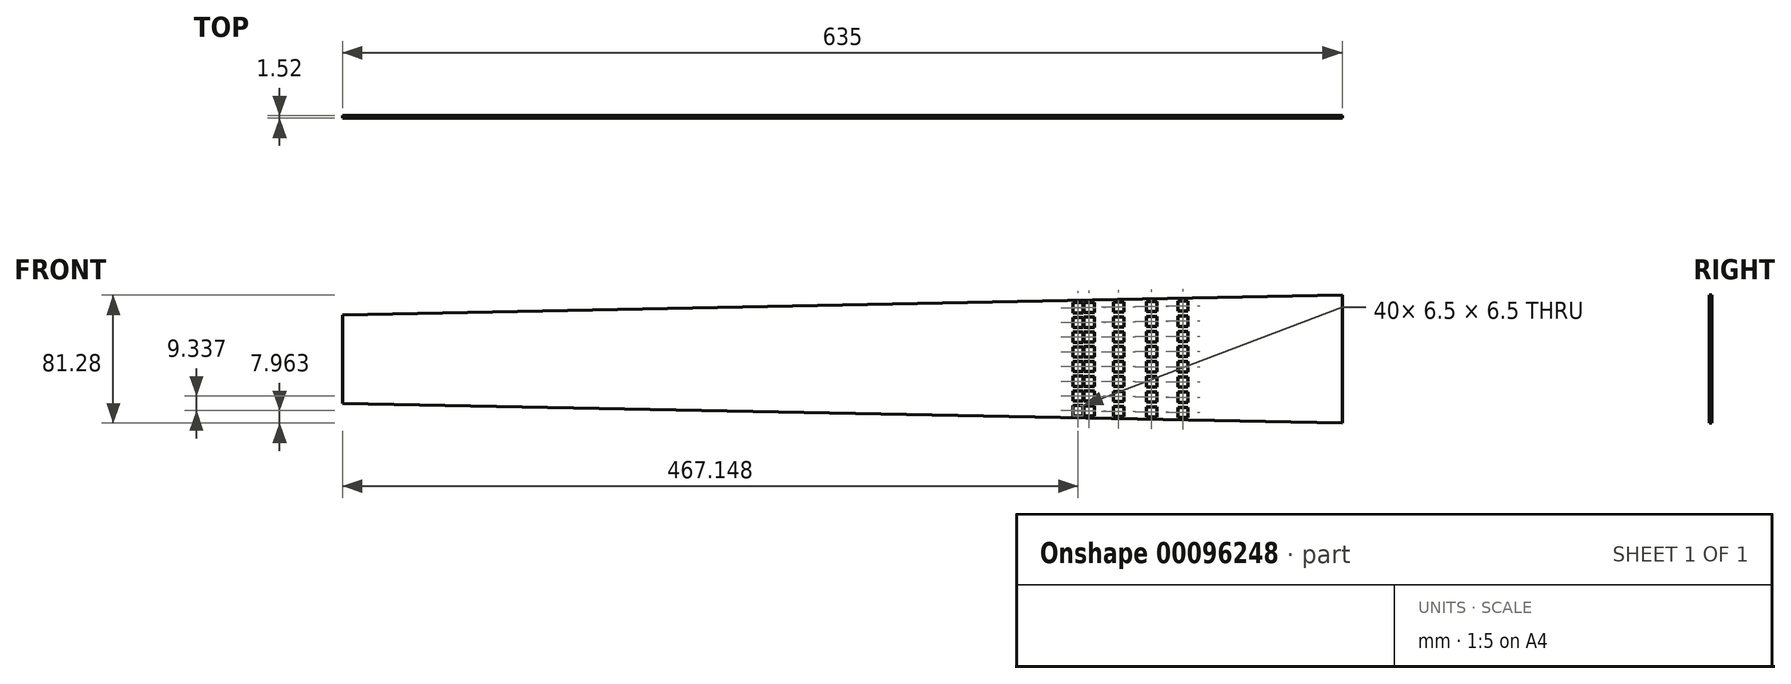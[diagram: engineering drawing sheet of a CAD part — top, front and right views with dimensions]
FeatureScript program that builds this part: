
annotation { "Feature Type Name" : "Feature", "Feature Type Description" : "" }
export const myFeature = defineFeature(function(context is Context, id is Id, definition is map)
    precondition{}
    {
        {
            var Q0;
            Q0=qCreatedBy(makeId("Front.planeOp"),FACE);
            var sketch = newSketch(context, id + "F0", { "sketchPlane" : qUnion([Q0])});
            skLineSegment(sketch, "E0", {"start": v(0, 0) * mm, "end": v(0, 56.39) * mm});
            skLineSegment(sketch, "E1", {"start": v(0, 56.39) * mm, "end": v(304.8, 62.36) * mm});
            skLineSegment(sketch, "E2", {"start": v(635, 68.83) * mm, "end": v(635, -12.45) * mm});
            skLineSegment(sketch, "E3", {"start": v(635, -12.45) * mm, "end": v(304.8, -5.97) * mm});
            skLineSegment(sketch, "E4", {"start": v(0, 28.2) * mm, "end": v(897.35, 28.2) * mm, "construction": true});
            skLineSegment(sketch, "E5", {"start": v(0, 3.52) * mm, "end": v(635, -7.37) * mm, "construction": true});
            skLineSegment(sketch, "E6", {"start": v(0, 10.57) * mm, "end": v(635, 2.8) * mm, "construction": true});
            skLineSegment(sketch, "E7", {"start": v(0, 17.62) * mm, "end": v(635, 12.95) * mm, "construction": true});
            skLineSegment(sketch, "E8", {"start": v(0, 24.67) * mm, "end": v(635, 23.11) * mm, "construction": true});
            skLineSegment(sketch, "E9", {"start": v(467.15, -27.86) * mm, "end": v(467.15, 72.83) * mm, "construction": true});
            skLineSegment(sketch, "E10", {"start": v(492.88, -29.16) * mm, "end": v(492.88, 78.06) * mm, "construction": true});
            skLineSegment(sketch, "E11", {"start": v(513.87, -22.04) * mm, "end": v(513.87, 76.59) * mm, "construction": true});
            skLineSegment(sketch, "E12", {"start": v(533.67, -25.93) * mm, "end": v(533.67, 79.32) * mm, "construction": true});
            skLineSegment(sketch, "E13", {"start": v(586.67, -17.8) * mm, "end": v(586.67, 83.9) * mm, "construction": true});
            skLineSegment(sketch, "E14", {"start": v(552.37, -18.5) * mm, "end": v(552.37, 94.16) * mm, "construction": true});
            skPoint(sketch, "E15", {"position": v(533.67, -5.63) * mm});
            skPoint(sketch, "E16", {"position": v(492.88, -4.93) * mm});
            skLineSegment(sketch, "E17.bottom", {"start": v(489.63, -1.68) * mm, "end": v(496.13, -1.68) * mm});
            skLineSegment(sketch, "E17.top", {"start": v(489.63, -8.18) * mm, "end": v(496.13, -8.18) * mm});
            skLineSegment(sketch, "E17.left", {"start": v(489.63, -1.68) * mm, "end": v(489.63, -8.18) * mm});
            skLineSegment(sketch, "E17.right", {"start": v(496.13, -1.68) * mm, "end": v(496.13, -8.18) * mm});
            skPoint(sketch, "E18", {"position": v(513.87, -5.29) * mm});
            skLineSegment(sketch, "E19.bottom", {"start": v(510.62, -2.04) * mm, "end": v(517.12, -2.04) * mm});
            skLineSegment(sketch, "E19.top", {"start": v(510.62, -8.54) * mm, "end": v(517.12, -8.54) * mm});
            skLineSegment(sketch, "E19.left", {"start": v(510.62, -2.04) * mm, "end": v(510.62, -8.54) * mm});
            skLineSegment(sketch, "E19.right", {"start": v(517.12, -2.04) * mm, "end": v(517.12, -8.54) * mm});
            skLineSegment(sketch, "E20.bottom", {"start": v(530.42, -2.38) * mm, "end": v(536.92, -2.38) * mm});
            skLineSegment(sketch, "E20.top", {"start": v(530.42, -8.88) * mm, "end": v(536.92, -8.88) * mm});
            skLineSegment(sketch, "E20.left", {"start": v(530.42, -2.38) * mm, "end": v(530.42, -8.88) * mm});
            skLineSegment(sketch, "E20.right", {"start": v(536.92, -2.38) * mm, "end": v(536.92, -8.88) * mm});
            skLineSegment(sketch, "E21", {"start": v(304.8, -5.97) * mm, "end": v(304.8, 62.36) * mm});
            skLineSegment(sketch, "E22", {"start": v(211.87, -18.15) * mm, "end": v(211.87, 88.54) * mm, "construction": true});
            skLineSegment(sketch, "E23", {"start": v(248.18, -17.72) * mm, "end": v(248.18, 84.91) * mm, "construction": true});
            skLineSegment(sketch, "E24", {"start": v(304.8, 62.36) * mm, "end": v(635, 68.83) * mm});
            skLineSegment(sketch, "E25", {"start": v(304.8, -5.97) * mm, "end": v(0, 0) * mm});
            skLineSegment(sketch, "E26", {"start": v(474.15, -18.13) * mm, "end": v(474.15, 73.32) * mm, "construction": true});
            skPoint(sketch, "E27", {"position": v(467.15, -4.49) * mm});
            skPoint(sketch, "E28", {"position": v(474.15, -4.6) * mm});
            skLineSegment(sketch, "E29.bottom", {"start": v(463.9, -1.24) * mm, "end": v(470.4, -1.24) * mm});
            skLineSegment(sketch, "E29.top", {"start": v(463.9, -7.74) * mm, "end": v(470.4, -7.74) * mm});
            skLineSegment(sketch, "E29.left", {"start": v(463.9, -1.24) * mm, "end": v(463.9, -7.74) * mm});
            skLineSegment(sketch, "E29.right", {"start": v(470.4, -1.24) * mm, "end": v(470.4, -7.74) * mm});
            skLineSegment(sketch, "E30.bottom", {"start": v(470.9, -1.36) * mm, "end": v(477.4, -1.36) * mm});
            skLineSegment(sketch, "E30.top", {"start": v(470.9, -7.86) * mm, "end": v(477.4, -7.86) * mm});
            skLineSegment(sketch, "E30.left", {"start": v(470.9, -1.36) * mm, "end": v(470.9, -7.86) * mm});
            skLineSegment(sketch, "E30.right", {"start": v(477.4, -1.36) * mm, "end": v(477.4, -7.86) * mm});
            skPoint(sketch, "E31", {"position": v(467.15, 4.85) * mm});
            skPoint(sketch, "E32", {"position": v(474.15, 4.76) * mm});
            skPoint(sketch, "E33", {"position": v(492.88, 4.53) * mm});
            skPoint(sketch, "E34", {"position": v(513.87, 4.28) * mm});
            skPoint(sketch, "E35", {"position": v(533.67, 4.04) * mm});
            skLineSegment(sketch, "E36.direction1", {"start": v(613.98, -10.31) * mm, "end": v(639.38, -10.31) * mm, "construction": true});
            skLineSegment(sketch, "E37.direction1", {"start": v(439.66, -0.82) * mm, "end": v(465.06, -0.82) * mm, "construction": true});
            skLineSegment(sketch, "E38.direction1", {"start": v(448.02, -7.47) * mm, "end": v(473.42, -7.47) * mm, "construction": true});
            skLineSegment(sketch, "E39.0.1.0", {"start": v(463.9, 8.1) * mm, "end": v(463.9, 1.6) * mm});
            skLineSegment(sketch, "E39.0.1.1", {"start": v(463.9, 1.6) * mm, "end": v(470.4, 1.6) * mm});
            skLineSegment(sketch, "E39.0.1.2", {"start": v(470.4, 8.1) * mm, "end": v(470.4, 1.6) * mm});
            skLineSegment(sketch, "E39.0.1.3", {"start": v(463.9, 8.1) * mm, "end": v(470.4, 8.1) * mm});
            skLineSegment(sketch, "E39.0.2.0", {"start": v(463.9, 17.44) * mm, "end": v(463.9, 10.94) * mm});
            skLineSegment(sketch, "E39.0.2.1", {"start": v(463.9, 10.94) * mm, "end": v(470.4, 10.94) * mm});
            skLineSegment(sketch, "E39.0.2.2", {"start": v(470.4, 17.44) * mm, "end": v(470.4, 10.94) * mm});
            skLineSegment(sketch, "E39.0.2.3", {"start": v(463.9, 17.44) * mm, "end": v(470.4, 17.44) * mm});
            skLineSegment(sketch, "E39.0.3.0", {"start": v(463.9, 26.77) * mm, "end": v(463.9, 20.27) * mm});
            skLineSegment(sketch, "E39.0.3.1", {"start": v(463.9, 20.27) * mm, "end": v(470.4, 20.27) * mm});
            skLineSegment(sketch, "E39.0.3.2", {"start": v(470.4, 26.77) * mm, "end": v(470.4, 20.27) * mm});
            skLineSegment(sketch, "E39.0.3.3", {"start": v(463.9, 26.77) * mm, "end": v(470.4, 26.77) * mm});
            skLineSegment(sketch, "E39.0.4.0", {"start": v(463.9, 36.11) * mm, "end": v(463.9, 29.61) * mm});
            skLineSegment(sketch, "E39.0.4.1", {"start": v(463.9, 29.61) * mm, "end": v(470.4, 29.61) * mm});
            skLineSegment(sketch, "E39.0.4.2", {"start": v(470.4, 36.11) * mm, "end": v(470.4, 29.61) * mm});
            skLineSegment(sketch, "E39.0.4.3", {"start": v(463.9, 36.11) * mm, "end": v(470.4, 36.11) * mm});
            skLineSegment(sketch, "E39.0.5.0", {"start": v(463.9, 45.45) * mm, "end": v(463.9, 38.95) * mm});
            skLineSegment(sketch, "E39.0.5.1", {"start": v(463.9, 38.95) * mm, "end": v(470.4, 38.95) * mm});
            skLineSegment(sketch, "E39.0.5.2", {"start": v(470.4, 45.45) * mm, "end": v(470.4, 38.95) * mm});
            skLineSegment(sketch, "E39.0.5.3", {"start": v(463.9, 45.45) * mm, "end": v(470.4, 45.45) * mm});
            skLineSegment(sketch, "E39.0.6.0", {"start": v(463.9, 54.78) * mm, "end": v(463.9, 48.28) * mm});
            skLineSegment(sketch, "E39.0.6.1", {"start": v(463.9, 48.28) * mm, "end": v(470.4, 48.28) * mm});
            skLineSegment(sketch, "E39.0.6.2", {"start": v(470.4, 54.78) * mm, "end": v(470.4, 48.28) * mm});
            skLineSegment(sketch, "E39.0.6.3", {"start": v(463.9, 54.78) * mm, "end": v(470.4, 54.78) * mm});
            skLineSegment(sketch, "E39.0.7.0", {"start": v(463.9, 64.12) * mm, "end": v(463.9, 57.62) * mm});
            skLineSegment(sketch, "E39.0.7.1", {"start": v(463.9, 57.62) * mm, "end": v(470.4, 57.62) * mm});
            skLineSegment(sketch, "E39.0.7.2", {"start": v(470.4, 64.12) * mm, "end": v(470.4, 57.62) * mm});
            skLineSegment(sketch, "E39.0.7.3", {"start": v(463.9, 64.12) * mm, "end": v(470.4, 64.12) * mm});
            skLineSegment(sketch, "E39.direction1", {"start": v(463.9, -7.74) * mm, "end": v(489.3, -7.74) * mm, "construction": true});
            skLineSegment(sketch, "E39.direction2", {"start": v(463.9, -7.74) * mm, "end": v(463.9, 1.6) * mm, "construction": true});
            skLineSegment(sketch, "E40.0.1.0", {"start": v(470.9, 8.02) * mm, "end": v(470.9, 1.52) * mm});
            skLineSegment(sketch, "E40.0.1.1", {"start": v(470.9, 8.02) * mm, "end": v(477.4, 8.02) * mm});
            skLineSegment(sketch, "E40.0.1.2", {"start": v(477.4, 8.02) * mm, "end": v(477.4, 1.52) * mm});
            skLineSegment(sketch, "E40.0.1.3", {"start": v(470.9, 1.52) * mm, "end": v(477.4, 1.52) * mm});
            skLineSegment(sketch, "E40.0.2.0", {"start": v(470.9, 17.39) * mm, "end": v(470.9, 10.89) * mm});
            skLineSegment(sketch, "E40.0.2.1", {"start": v(470.9, 17.39) * mm, "end": v(477.4, 17.39) * mm});
            skLineSegment(sketch, "E40.0.2.2", {"start": v(477.4, 17.39) * mm, "end": v(477.4, 10.89) * mm});
            skLineSegment(sketch, "E40.0.2.3", {"start": v(470.9, 10.89) * mm, "end": v(477.4, 10.89) * mm});
            skLineSegment(sketch, "E40.0.3.0", {"start": v(470.9, 26.76) * mm, "end": v(470.9, 20.26) * mm});
            skLineSegment(sketch, "E40.0.3.1", {"start": v(470.9, 26.76) * mm, "end": v(477.4, 26.76) * mm});
            skLineSegment(sketch, "E40.0.3.2", {"start": v(477.4, 26.76) * mm, "end": v(477.4, 20.26) * mm});
            skLineSegment(sketch, "E40.0.3.3", {"start": v(470.9, 20.26) * mm, "end": v(477.4, 20.26) * mm});
            skLineSegment(sketch, "E40.0.4.0", {"start": v(470.9, 36.13) * mm, "end": v(470.9, 29.63) * mm});
            skLineSegment(sketch, "E40.0.4.1", {"start": v(470.9, 36.13) * mm, "end": v(477.4, 36.13) * mm});
            skLineSegment(sketch, "E40.0.4.2", {"start": v(477.4, 36.13) * mm, "end": v(477.4, 29.63) * mm});
            skLineSegment(sketch, "E40.0.4.3", {"start": v(470.9, 29.63) * mm, "end": v(477.4, 29.63) * mm});
            skLineSegment(sketch, "E40.0.5.0", {"start": v(470.9, 45.5) * mm, "end": v(470.9, 39) * mm});
            skLineSegment(sketch, "E40.0.5.1", {"start": v(470.9, 45.5) * mm, "end": v(477.4, 45.5) * mm});
            skLineSegment(sketch, "E40.0.5.2", {"start": v(477.4, 45.5) * mm, "end": v(477.4, 39) * mm});
            skLineSegment(sketch, "E40.0.5.3", {"start": v(470.9, 39) * mm, "end": v(477.4, 39) * mm});
            skLineSegment(sketch, "E40.0.6.0", {"start": v(470.9, 54.88) * mm, "end": v(470.9, 48.38) * mm});
            skLineSegment(sketch, "E40.0.6.1", {"start": v(470.9, 54.88) * mm, "end": v(477.4, 54.88) * mm});
            skLineSegment(sketch, "E40.0.6.2", {"start": v(477.4, 54.88) * mm, "end": v(477.4, 48.38) * mm});
            skLineSegment(sketch, "E40.0.6.3", {"start": v(470.9, 48.38) * mm, "end": v(477.4, 48.38) * mm});
            skLineSegment(sketch, "E40.0.7.0", {"start": v(470.9, 64.25) * mm, "end": v(470.9, 57.75) * mm});
            skLineSegment(sketch, "E40.0.7.1", {"start": v(470.9, 64.25) * mm, "end": v(477.4, 64.25) * mm});
            skLineSegment(sketch, "E40.0.7.2", {"start": v(477.4, 64.25) * mm, "end": v(477.4, 57.75) * mm});
            skLineSegment(sketch, "E40.0.7.3", {"start": v(470.9, 57.75) * mm, "end": v(477.4, 57.75) * mm});
            skLineSegment(sketch, "E40.direction1", {"start": v(470.9, -7.86) * mm, "end": v(496.3, -7.86) * mm, "construction": true});
            skLineSegment(sketch, "E40.direction2", {"start": v(470.9, -7.86) * mm, "end": v(470.9, 1.52) * mm, "construction": true});
            skLineSegment(sketch, "E41.0.1.0", {"start": v(489.63, 7.79) * mm, "end": v(489.63, 1.29) * mm});
            skLineSegment(sketch, "E41.0.1.1", {"start": v(496.13, 7.79) * mm, "end": v(496.13, 1.29) * mm});
            skLineSegment(sketch, "E41.0.1.2", {"start": v(489.63, 7.79) * mm, "end": v(496.13, 7.79) * mm});
            skLineSegment(sketch, "E41.0.1.3", {"start": v(489.63, 1.29) * mm, "end": v(496.13, 1.29) * mm});
            skLineSegment(sketch, "E41.0.2.0", {"start": v(489.63, 17.25) * mm, "end": v(489.63, 10.75) * mm});
            skLineSegment(sketch, "E41.0.2.1", {"start": v(496.13, 17.25) * mm, "end": v(496.13, 10.75) * mm});
            skLineSegment(sketch, "E41.0.2.2", {"start": v(489.63, 17.25) * mm, "end": v(496.13, 17.25) * mm});
            skLineSegment(sketch, "E41.0.2.3", {"start": v(489.63, 10.75) * mm, "end": v(496.13, 10.75) * mm});
            skLineSegment(sketch, "E41.0.3.0", {"start": v(489.63, 26.71) * mm, "end": v(489.63, 20.21) * mm});
            skLineSegment(sketch, "E41.0.3.1", {"start": v(496.13, 26.71) * mm, "end": v(496.13, 20.21) * mm});
            skLineSegment(sketch, "E41.0.3.2", {"start": v(489.63, 26.71) * mm, "end": v(496.13, 26.71) * mm});
            skLineSegment(sketch, "E41.0.3.3", {"start": v(489.63, 20.21) * mm, "end": v(496.13, 20.21) * mm});
            skLineSegment(sketch, "E41.0.4.0", {"start": v(489.63, 36.18) * mm, "end": v(489.63, 29.68) * mm});
            skLineSegment(sketch, "E41.0.4.1", {"start": v(496.13, 36.18) * mm, "end": v(496.13, 29.68) * mm});
            skLineSegment(sketch, "E41.0.4.2", {"start": v(489.63, 36.18) * mm, "end": v(496.13, 36.18) * mm});
            skLineSegment(sketch, "E41.0.4.3", {"start": v(489.63, 29.68) * mm, "end": v(496.13, 29.68) * mm});
            skLineSegment(sketch, "E41.0.5.0", {"start": v(489.63, 45.64) * mm, "end": v(489.63, 39.14) * mm});
            skLineSegment(sketch, "E41.0.5.1", {"start": v(496.13, 45.64) * mm, "end": v(496.13, 39.14) * mm});
            skLineSegment(sketch, "E41.0.5.2", {"start": v(489.63, 45.64) * mm, "end": v(496.13, 45.64) * mm});
            skLineSegment(sketch, "E41.0.5.3", {"start": v(489.63, 39.14) * mm, "end": v(496.13, 39.14) * mm});
            skLineSegment(sketch, "E41.0.6.0", {"start": v(489.63, 55.1) * mm, "end": v(489.63, 48.6) * mm});
            skLineSegment(sketch, "E41.0.6.1", {"start": v(496.13, 55.1) * mm, "end": v(496.13, 48.6) * mm});
            skLineSegment(sketch, "E41.0.6.2", {"start": v(489.63, 55.1) * mm, "end": v(496.13, 55.1) * mm});
            skLineSegment(sketch, "E41.0.6.3", {"start": v(489.63, 48.6) * mm, "end": v(496.13, 48.6) * mm});
            skLineSegment(sketch, "E41.0.7.0", {"start": v(489.63, 64.57) * mm, "end": v(489.63, 58.07) * mm});
            skLineSegment(sketch, "E41.0.7.1", {"start": v(496.13, 64.57) * mm, "end": v(496.13, 58.07) * mm});
            skLineSegment(sketch, "E41.0.7.2", {"start": v(489.63, 64.57) * mm, "end": v(496.13, 64.57) * mm});
            skLineSegment(sketch, "E41.0.7.3", {"start": v(489.63, 58.07) * mm, "end": v(496.13, 58.07) * mm});
            skLineSegment(sketch, "E41.direction1", {"start": v(489.63, -8.18) * mm, "end": v(515.03, -8.18) * mm, "construction": true});
            skLineSegment(sketch, "E41.direction2", {"start": v(489.63, -8.18) * mm, "end": v(489.63, 1.29) * mm, "construction": true});
            skLineSegment(sketch, "E42.0.1.0", {"start": v(510.62, 7.53) * mm, "end": v(510.62, 1.03) * mm});
            skLineSegment(sketch, "E42.0.1.1", {"start": v(510.62, 7.53) * mm, "end": v(517.12, 7.53) * mm});
            skLineSegment(sketch, "E42.0.1.2", {"start": v(510.62, 1.03) * mm, "end": v(517.12, 1.03) * mm});
            skLineSegment(sketch, "E42.0.1.3", {"start": v(517.12, 7.53) * mm, "end": v(517.12, 1.03) * mm});
            skLineSegment(sketch, "E42.0.2.0", {"start": v(510.62, 17.1) * mm, "end": v(510.62, 10.6) * mm});
            skLineSegment(sketch, "E42.0.2.1", {"start": v(510.62, 17.1) * mm, "end": v(517.12, 17.1) * mm});
            skLineSegment(sketch, "E42.0.2.2", {"start": v(510.62, 10.6) * mm, "end": v(517.12, 10.6) * mm});
            skLineSegment(sketch, "E42.0.2.3", {"start": v(517.12, 17.1) * mm, "end": v(517.12, 10.6) * mm});
            skLineSegment(sketch, "E42.0.3.0", {"start": v(510.62, 26.66) * mm, "end": v(510.62, 20.16) * mm});
            skLineSegment(sketch, "E42.0.3.1", {"start": v(510.62, 26.66) * mm, "end": v(517.12, 26.66) * mm});
            skLineSegment(sketch, "E42.0.3.2", {"start": v(510.62, 20.16) * mm, "end": v(517.12, 20.16) * mm});
            skLineSegment(sketch, "E42.0.3.3", {"start": v(517.12, 26.66) * mm, "end": v(517.12, 20.16) * mm});
            skLineSegment(sketch, "E42.0.4.0", {"start": v(510.62, 36.22) * mm, "end": v(510.62, 29.72) * mm});
            skLineSegment(sketch, "E42.0.4.1", {"start": v(510.62, 36.22) * mm, "end": v(517.12, 36.22) * mm});
            skLineSegment(sketch, "E42.0.4.2", {"start": v(510.62, 29.72) * mm, "end": v(517.12, 29.72) * mm});
            skLineSegment(sketch, "E42.0.4.3", {"start": v(517.12, 36.22) * mm, "end": v(517.12, 29.72) * mm});
            skLineSegment(sketch, "E42.0.5.0", {"start": v(510.62, 45.79) * mm, "end": v(510.62, 39.29) * mm});
            skLineSegment(sketch, "E42.0.5.1", {"start": v(510.62, 45.79) * mm, "end": v(517.12, 45.79) * mm});
            skLineSegment(sketch, "E42.0.5.2", {"start": v(510.62, 39.29) * mm, "end": v(517.12, 39.29) * mm});
            skLineSegment(sketch, "E42.0.5.3", {"start": v(517.12, 45.79) * mm, "end": v(517.12, 39.29) * mm});
            skLineSegment(sketch, "E42.0.6.0", {"start": v(510.62, 55.36) * mm, "end": v(510.62, 48.86) * mm});
            skLineSegment(sketch, "E42.0.6.1", {"start": v(510.62, 55.36) * mm, "end": v(517.12, 55.36) * mm});
            skLineSegment(sketch, "E42.0.6.2", {"start": v(510.62, 48.86) * mm, "end": v(517.12, 48.86) * mm});
            skLineSegment(sketch, "E42.0.6.3", {"start": v(517.12, 55.36) * mm, "end": v(517.12, 48.86) * mm});
            skLineSegment(sketch, "E42.0.7.0", {"start": v(510.62, 64.92) * mm, "end": v(510.62, 58.42) * mm});
            skLineSegment(sketch, "E42.0.7.1", {"start": v(510.62, 64.92) * mm, "end": v(517.12, 64.92) * mm});
            skLineSegment(sketch, "E42.0.7.2", {"start": v(510.62, 58.42) * mm, "end": v(517.12, 58.42) * mm});
            skLineSegment(sketch, "E42.0.7.3", {"start": v(517.12, 64.92) * mm, "end": v(517.12, 58.42) * mm});
            skLineSegment(sketch, "E42.direction1", {"start": v(510.62, -8.54) * mm, "end": v(536.02, -8.54) * mm, "construction": true});
            skLineSegment(sketch, "E42.direction2", {"start": v(510.62, -8.54) * mm, "end": v(510.62, 1.03) * mm, "construction": true});
            skLineSegment(sketch, "E43.0.1.0", {"start": v(530.42, 7.29) * mm, "end": v(530.42, 0.79) * mm});
            skLineSegment(sketch, "E43.0.1.1", {"start": v(530.42, 0.79) * mm, "end": v(536.92, 0.79) * mm});
            skLineSegment(sketch, "E43.0.1.2", {"start": v(536.92, 7.29) * mm, "end": v(536.92, 0.79) * mm});
            skLineSegment(sketch, "E43.0.1.3", {"start": v(530.42, 7.29) * mm, "end": v(536.92, 7.29) * mm});
            skLineSegment(sketch, "E43.0.2.0", {"start": v(530.42, 16.95) * mm, "end": v(530.42, 10.45) * mm});
            skLineSegment(sketch, "E43.0.2.1", {"start": v(530.42, 10.45) * mm, "end": v(536.92, 10.45) * mm});
            skLineSegment(sketch, "E43.0.2.2", {"start": v(536.92, 16.95) * mm, "end": v(536.92, 10.45) * mm});
            skLineSegment(sketch, "E43.0.2.3", {"start": v(530.42, 16.95) * mm, "end": v(536.92, 16.95) * mm});
            skLineSegment(sketch, "E43.0.3.0", {"start": v(530.42, 26.62) * mm, "end": v(530.42, 20.12) * mm});
            skLineSegment(sketch, "E43.0.3.1", {"start": v(530.42, 20.12) * mm, "end": v(536.92, 20.12) * mm});
            skLineSegment(sketch, "E43.0.3.2", {"start": v(536.92, 26.62) * mm, "end": v(536.92, 20.12) * mm});
            skLineSegment(sketch, "E43.0.3.3", {"start": v(530.42, 26.62) * mm, "end": v(536.92, 26.62) * mm});
            skLineSegment(sketch, "E43.0.4.0", {"start": v(530.42, 36.28) * mm, "end": v(530.42, 29.78) * mm});
            skLineSegment(sketch, "E43.0.4.1", {"start": v(530.42, 29.78) * mm, "end": v(536.92, 29.78) * mm});
            skLineSegment(sketch, "E43.0.4.2", {"start": v(536.92, 36.28) * mm, "end": v(536.92, 29.78) * mm});
            skLineSegment(sketch, "E43.0.4.3", {"start": v(530.42, 36.28) * mm, "end": v(536.92, 36.28) * mm});
            skLineSegment(sketch, "E43.0.5.0", {"start": v(530.42, 45.95) * mm, "end": v(530.42, 39.45) * mm});
            skLineSegment(sketch, "E43.0.5.1", {"start": v(530.42, 39.45) * mm, "end": v(536.92, 39.45) * mm});
            skLineSegment(sketch, "E43.0.5.2", {"start": v(536.92, 45.95) * mm, "end": v(536.92, 39.45) * mm});
            skLineSegment(sketch, "E43.0.5.3", {"start": v(530.42, 45.95) * mm, "end": v(536.92, 45.95) * mm});
            skLineSegment(sketch, "E43.0.6.0", {"start": v(530.42, 55.6) * mm, "end": v(530.42, 49.1) * mm});
            skLineSegment(sketch, "E43.0.6.1", {"start": v(530.42, 49.1) * mm, "end": v(536.92, 49.1) * mm});
            skLineSegment(sketch, "E43.0.6.2", {"start": v(536.92, 55.6) * mm, "end": v(536.92, 49.1) * mm});
            skLineSegment(sketch, "E43.0.6.3", {"start": v(530.42, 55.6) * mm, "end": v(536.92, 55.6) * mm});
            skLineSegment(sketch, "E43.0.7.0", {"start": v(530.42, 65.27) * mm, "end": v(530.42, 58.77) * mm});
            skLineSegment(sketch, "E43.0.7.1", {"start": v(530.42, 58.77) * mm, "end": v(536.92, 58.77) * mm});
            skLineSegment(sketch, "E43.0.7.2", {"start": v(536.92, 65.27) * mm, "end": v(536.92, 58.77) * mm});
            skLineSegment(sketch, "E43.0.7.3", {"start": v(530.42, 65.27) * mm, "end": v(536.92, 65.27) * mm});
            skLineSegment(sketch, "E43.direction1", {"start": v(530.42, -8.88) * mm, "end": v(555.82, -8.88) * mm, "construction": true});
            skLineSegment(sketch, "E43.direction2", {"start": v(530.42, -8.88) * mm, "end": v(530.42, 0.79) * mm, "construction": true});
            skSolve(sketch);
        }
        {
            var Q0;
            Q0=qSketchRegion(id+"F0",true);
            extrude(context, id + "F1", {"entities" : qUnion([Q0]), "depth" : 1.52 * mm});
        }
        {
            var Q0;
            Q0=makeQuery(id+"F1.opExtrude","CAP_FACE",FACE,{"disambiguationData":[OSD([sQuery(id+"F0.wireOp",EDGE,"E0"),sQuery(id+"F0.wireOp",EDGE,"E1"),sQuery(id+"F0.wireOp",EDGE,"E2"),sQuery(id+"F0.wireOp",EDGE,"E3")])],"isStart":false});
            var sketch = newSketch(context, id + "F2", { "sketchPlane" : qUnion([Q0])});
            skLineSegment(sketch, "E44", {"start": v(0, 28.2) * mm, "end": v(635, 28.2) * mm, "construction": true});
            skSolve(sketch);
        }
        {
            var Q0;
            Q0=makeQuery(id+"F2.imprint","IMPRINT",FACE,{"disambiguationData":[TD([[makeQuery(id+"F2.imprint","IMPRINT",EDGE,{"derivedFrom":makeQuery(id+"F1.opExtrude","CAP_EDGE",EDGE,{"disambiguationData":[OSD([sQuery(id+"F0.wireOp",EDGE,"E0")])],"isStart":false})}),-1.0]])]});
            var sketch = newSketch(context, id + "F3", { "sketchPlane" : qUnion([Q0])});
            skCircle(sketch, "E45", {"center": v(97.4, 8.08) * mm, "radius": 1.13 * mm});
            skLineSegment(sketch, "E46", {"start": v(0, 8.12) * mm, "end": v(635, 7.87) * mm, "construction": true});
            skCircle(sketch, "E47", {"center": v(3.18, 8.12) * mm, "radius": 1.13 * mm});
            skCircle(sketch, "E48", {"center": v(181.33, 8.05) * mm, "radius": 1.13 * mm});
            skCircle(sketch, "E49", {"center": v(290.4, 8) * mm, "radius": 1.13 * mm});
            skCircle(sketch, "E50", {"center": v(409.3, 7.96) * mm, "radius": 1.13 * mm});
            skCircle(sketch, "E51", {"center": v(524.06, 7.92) * mm, "radius": 1.13 * mm});
            skCircle(sketch, "E52", {"center": v(624.44, 7.88) * mm, "radius": 1.13 * mm});
            skCircle(sketch, "E53.MirrorC", {"center": v(97.4, 48.3) * mm, "radius": 1.13 * mm});
            skCircle(sketch, "E54.MirrorC", {"center": v(3.18, 48.27) * mm, "radius": 1.13 * mm});
            skCircle(sketch, "E55.MirrorC", {"center": v(181.33, 48.34) * mm, "radius": 1.13 * mm});
            skCircle(sketch, "E56.MirrorC", {"center": v(290.4, 48.38) * mm, "radius": 1.13 * mm});
            skCircle(sketch, "E57.MirrorC", {"center": v(409.3, 48.43) * mm, "radius": 1.13 * mm});
            skCircle(sketch, "E58.MirrorC", {"center": v(524.06, 48.47) * mm, "radius": 1.13 * mm});
            skCircle(sketch, "E59.MirrorC", {"center": v(624.44, 48.5) * mm, "radius": 1.13 * mm});
            skSolve(sketch);
        }
        {
            var Q0;
            Q0=qSketchRegion(id+"F3",true);
            extrude(context, id + "F4", {"entities" : qUnion([Q0]), "operationType" : NewBodyOperationType.REMOVE, "endBound" : BoundingType.THROUGH_ALL, "depth" : 25.4 * mm});
        }
    });
